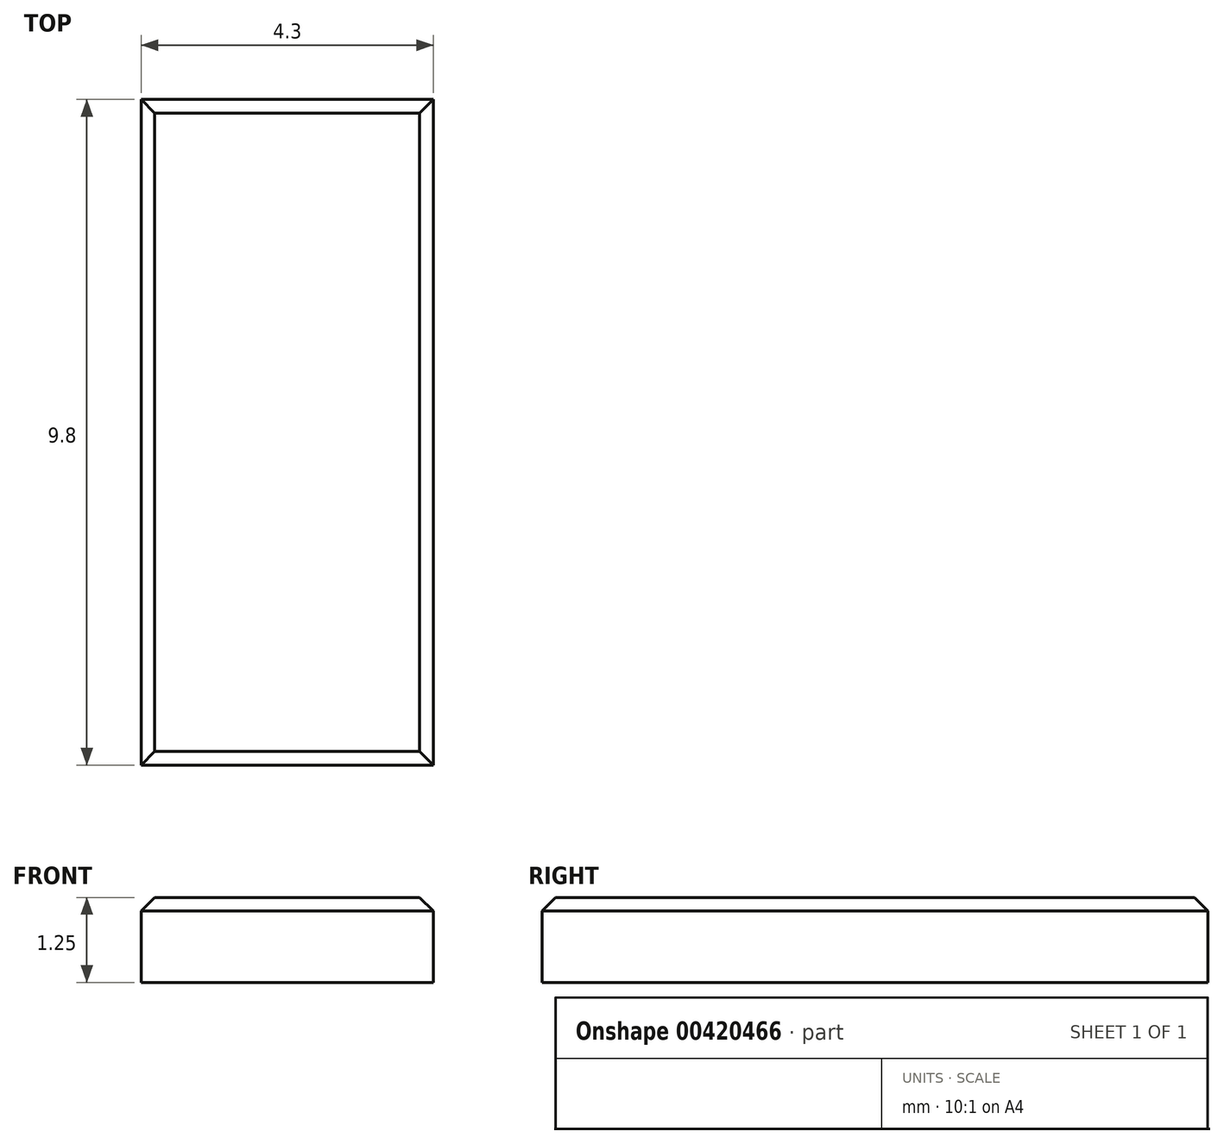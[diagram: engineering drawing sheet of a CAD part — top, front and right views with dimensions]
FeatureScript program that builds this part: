
annotation { "Feature Type Name" : "Feature", "Feature Type Description" : "" }
export const myFeature = defineFeature(function(context is Context, id is Id, definition is map)
    precondition{}
    {
        {
            var Q0;
            Q0=qCreatedBy(makeId("Top.planeOp"),FACE);
            var sketch = newSketch(context, id + "F0", { "sketchPlane" : qUnion([Q0])});
            skLineSegment(sketch, "E0.bottom", {"start": v(0, 0) * mm, "end": v(4.3, 0) * mm});
            skLineSegment(sketch, "E0.top", {"start": v(0, 9.8) * mm, "end": v(4.3, 9.8) * mm});
            skLineSegment(sketch, "E0.left", {"start": v(0, 0) * mm, "end": v(0, 9.8) * mm});
            skLineSegment(sketch, "E0.right", {"start": v(4.3, 0) * mm, "end": v(4.3, 9.8) * mm});
            skSolve(sketch);
        }
        {
            var Q0;
            Q0 = qSketchRegion(id + "F0", true);
            extrude(context, id + "F1", {"entities" : qUnion([Q0]), "depth" : 1.25 * mm});
        }
        {
            var Q0;
            Q0=makeQuery(id+"F1.opExtrude","CAP_EDGE",EDGE,{"disambiguationData":[OSD([sQuery(id+"F0.wireOp",EDGE,"E0.top")])],"isStart":false});
            var Q1;
            Q1=makeQuery(id+"F1.opExtrude","CAP_EDGE",EDGE,{"disambiguationData":[OSD([sQuery(id+"F0.wireOp",EDGE,"E0.left")])],"isStart":false});
            var Q2;
            Q2=makeQuery(id+"F1.opExtrude","CAP_EDGE",EDGE,{"disambiguationData":[OSD([sQuery(id+"F0.wireOp",EDGE,"E0.right")])],"isStart":false});
            var Q3;
            Q3=makeQuery(id+"F1.opExtrude","CAP_EDGE",EDGE,{"disambiguationData":[OSD([sQuery(id+"F0.wireOp",EDGE,"E0.bottom")])],"isStart":false});
            chamfer(context, id + "F2", {"entities" : qUnion([Q0, Q1, Q2, Q3]), "width" : 0.2 * mm, "tangentPropagation" : true});
        }
    });
